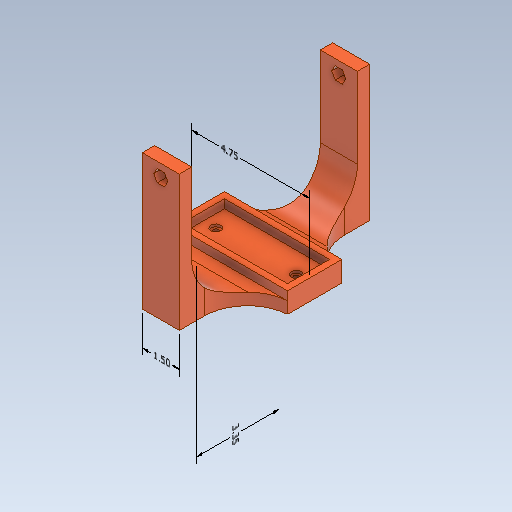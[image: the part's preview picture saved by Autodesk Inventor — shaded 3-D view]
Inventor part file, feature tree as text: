
AUTODESK INVENTOR PART (.ipt)
format: ipt  version: 2021.2 (Build 252289000, 289)  size: 230,400 bytes
history: native  units: in
note: dims shown in document units (in); Inventor stores cm internally (conversion verified against a paired STEP export)
features: sketch x5, extrude x5, other x4, fillet x2, hole x1, mirror x1
ambient origin geometry x8: Origin, YZ Plane, XZ Plane, XY Plane, X Axis, Y Axis, Z Axis, Center Point
bodies: Solid1 (feature_tree)
feature tree (18):
  other  "Annotations"
  sketch  "Sketch1"  dims[d0=1.7in d1=4.25in]
  extrude  "Extrusion1"  Depth=4.25in
  extrude  "Extrusion2"  Depth=0.25in
  hole  "Hole1"  [1 undecoded]
  extrude  "Extrusion10"  TaperAngle=0.0deg  [1 undecoded]
  extrude  "Extrusion11"  Depth=1.75in
  extrude  "Extrusion12"  Depth=1.75in
  mirror  "Mirror8"
  fillet  "Fillet1"  Radius=0.375in
  fillet  "Fillet2"  Radius=2.75in
  sketch  "Sketch2"  dims[d2=0.25in d3=0.25in]
  sketch  "Sketch15"  dims[d4=0.475in d5=0.0in]
  sketch  "Sketch16"  dims[d6=0.35in d7=0.0in]
  sketch  "Sketch17"  dims[d8=0.5in d9=0.5in d10=0.201in d11=0.75in d12=0.4in d13=0.1in d14=0.5635in d15=1.0in d16=0.8108in d17=0.375in d24=0.375in d101=2.75in d102=0.0in d103=0.5in d104=5.0in d105=0.0in d109=1.5in d115=0.0in d116=0.0in d117=1.75in d118=1.75in d119=0.5in d120=0.5in d106=0.9428in d107=4.2237in d108=3.35in d110=0.3497in d111=0.335in d112=1.5in d92=0.237in d93=0.16in d94=4.75in d121=0.5in d122=0.0344in]
  other  "Linear Dimension 1"
  other  "Linear Dimension 4"
  other  "Linear Dimension 5"
note: 2 required parameter values undecoded (feature->parameter linkage not recoverable at this tier; creation-order binding heuristic only, values carry confidence <= 0.55)
